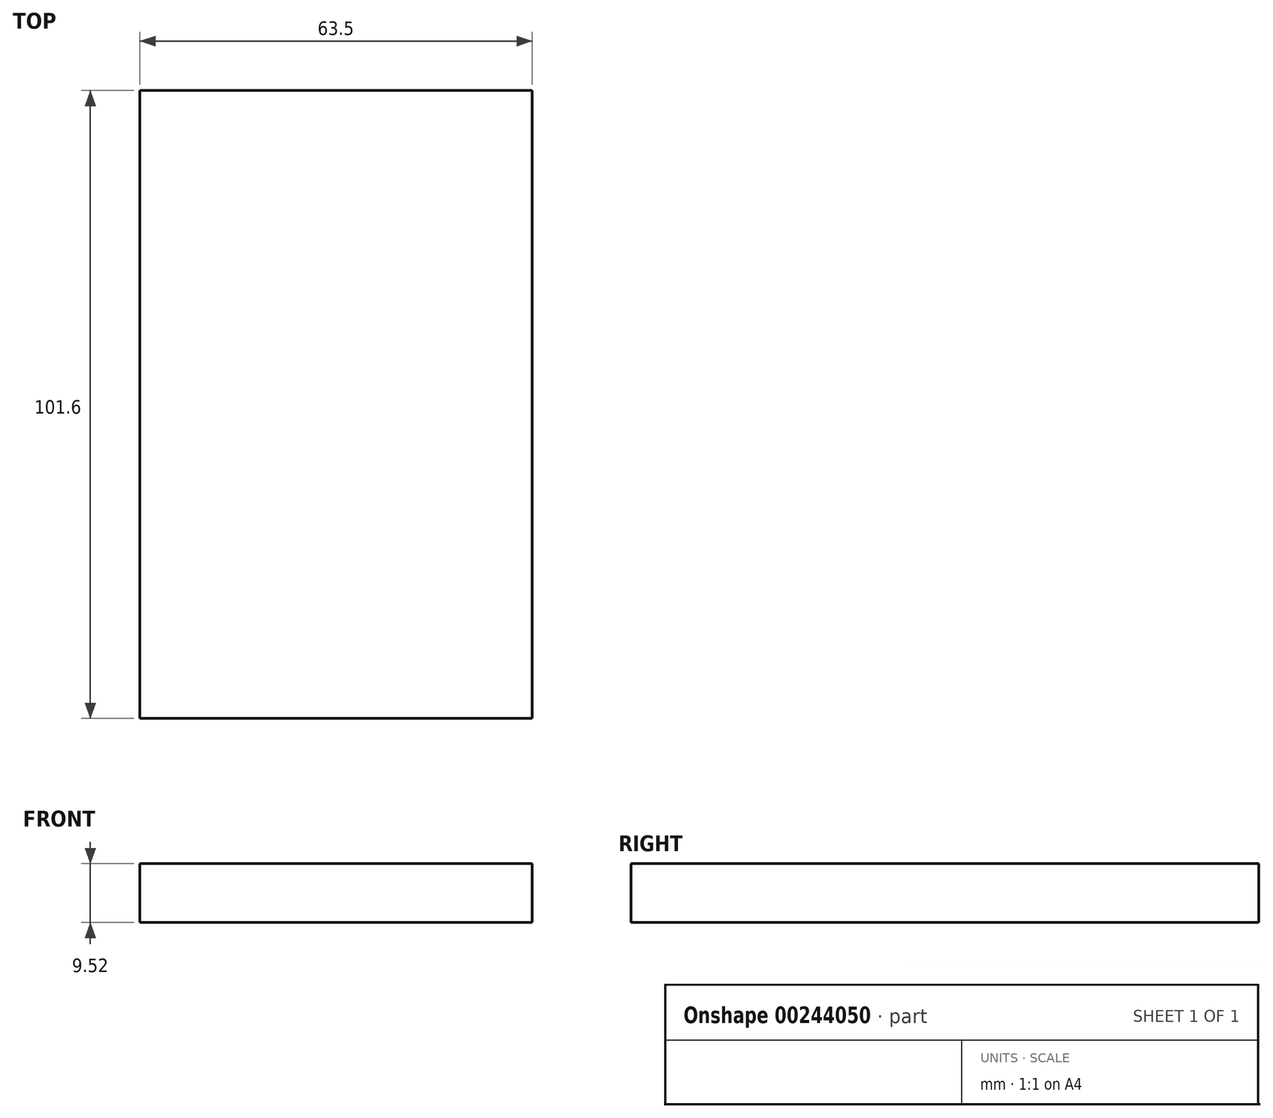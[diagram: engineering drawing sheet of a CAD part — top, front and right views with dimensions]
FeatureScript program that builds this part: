
annotation { "Feature Type Name" : "Feature", "Feature Type Description" : "" }
export const myFeature = defineFeature(function(context is Context, id is Id, definition is map)
    precondition{}
    {
        {
            var Q0;
            Q0=qCreatedBy(makeId("Front.planeOp"),FACE);
            var sketch = newSketch(context, id + "F0", { "sketchPlane" : qUnion([Q0])});
            skLineSegment(sketch, "E0.bottom", {"start": v(31.75, 6.35) * mm, "end": v(-31.75, 6.35) * mm});
            skLineSegment(sketch, "E0.top", {"start": v(31.75, -6.35) * mm, "end": v(-31.75, -6.35) * mm});
            skLineSegment(sketch, "E0.left", {"start": v(31.75, 6.35) * mm, "end": v(31.75, -6.35) * mm});
            skLineSegment(sketch, "E0.right", {"start": v(-31.75, 6.35) * mm, "end": v(-31.75, -6.35) * mm});
            skPoint(sketch, "E0.middle", {"position": v(0, 0) * mm});
            skLineSegment(sketch, "E1", {"start": v(-31.75, 3.17) * mm, "end": v(31.75, 3.18) * mm});
            skLineSegment(sketch, "E2", {"start": v(-25.4, 6.35) * mm, "end": v(-25.4, 3.17) * mm});
            skLineSegment(sketch, "E3", {"start": v(25.4, 6.35) * mm, "end": v(25.4, 3.18) * mm});
            skLineSegment(sketch, "E4", {"start": v(-28.57, 6.35) * mm, "end": v(-28.57, 3.17) * mm});
            skLineSegment(sketch, "E5", {"start": v(28.57, 6.35) * mm, "end": v(28.57, 3.18) * mm});
            skArc(sketch, "E6", {"start": v(-25.4, 3.17) * mm, "mid": v(-26.33, 5.42) * mm, "end": v(-28.57, 6.35) * mm});
            skArc(sketch, "E7", {"start": v(28.57, 6.35) * mm, "mid": v(26.33, 5.42) * mm, "end": v(25.4, 3.18) * mm});
            skSolve(sketch);
        }
        {
            var Q0;
            {var subQ4=sQuery(id+"F0.wireOp",EDGE,"E0.top");Q0=makeQuery(id+"F0.imprint","IMPRINT",FACE,{"disambiguationData":[TD([[makeQuery(id+"F0.imprint","IMPRINT",EDGE,{"derivedFrom":subQ4}),-1.0]])]});}
            extrude(context, id + "F1", {"entities" : qUnion([Q0]), "endBound" : BoundingType.SYMMETRIC, "depth" : 101.6 * mm});
        }
        {
            var Q0;
            Q0=qCreatedBy(makeId("Front.planeOp"),FACE);
            var sketch = newSketch(context, id + "F2", { "sketchPlane" : qUnion([Q0])});
            skFitSpline(sketch, "E8", {"points": [v(-61.64, 30.82) * mm, v(-48.28, 42.05) * mm, v(-30.97, 34.46) * mm, v(-10.32, 43.27) * mm, v(23.99, 34.77) * mm, v(18.52, 31.43) * mm, v(26.11, 21.4) * mm], "startDerivative": vector(74.38, 104.93) * mm, "endDerivative": vector(97.61, -84.85) * mm});
            skSolve(sketch);
        }
    });
